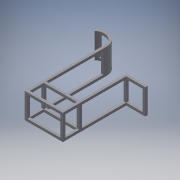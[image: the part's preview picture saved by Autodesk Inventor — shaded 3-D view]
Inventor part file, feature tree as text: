
AUTODESK INVENTOR PART (.ipt)
format: ipt  version: 2017 (Build 210142000, 142)  size: 224,256 bytes
history: native  units: mm
features: extrude x4, sketch x3, projected_geometry x1
ambient origin geometry x8: Origin, YZ Plane, XZ Plane, XY Plane, X Axis, Y Axis, Z Axis, Center Point
bodies: Solid1 (feature_tree)
feature tree (8):
  extrude  "Extrusion1"  Depth=40.0mm
  extrude  "Extrusion2"  Depth=40.0mm
  extrude  "Extrusion3"  Depth=600.0mm
  extrude  "Extrusion4"  Depth=300.0mm
  sketch  "Sketch2"  dims[d0=40.0mm d1=40.0mm]
  sketch  "Sketch3"  dims[d2=40.0mm d3=40.0mm]
  sketch  "Sketch4"  dims[d4=40.0mm d6=600.0mm d7=1400.0mm d8=1000.0mm d9=300.0mm d12=400.0mm d13=0.0mm d14=40.0mm d15=40.0mm d16=40.0mm d17=40.0mm d18=40.0mm d19=40.0mm d20=400.0mm d21=0.0mm d22=40.0mm d23=40.0mm d24=160.284942mm d25=400.0mm d26=0.0mm d27=10.0mm d28=0.0mm d29=200.0mm d30=300.0mm]
  projected_geometry  "Projected Loop1"
